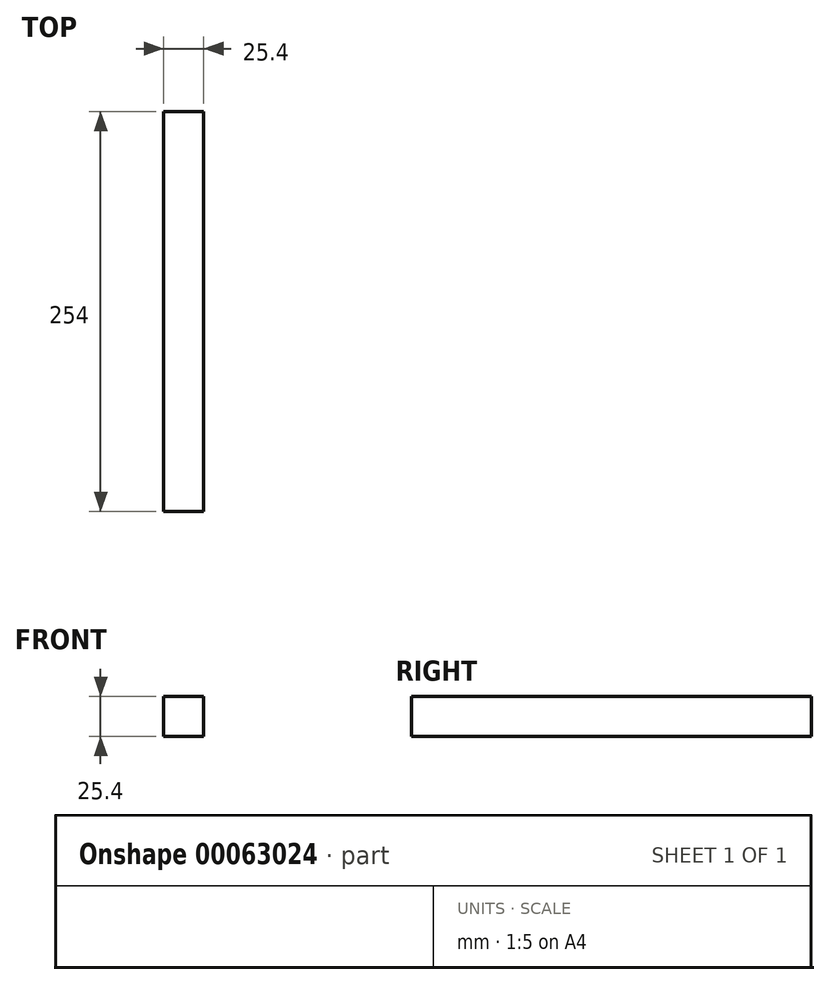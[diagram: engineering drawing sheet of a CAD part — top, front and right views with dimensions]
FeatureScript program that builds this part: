
annotation { "Feature Type Name" : "Feature", "Feature Type Description" : "" }
export const myFeature = defineFeature(function(context is Context, id is Id, definition is map)
    precondition{}
    {
        {
            var Q0;
            Q0=qCreatedBy(makeId("Top.planeOp"),FACE);
            var sketch = newSketch(context, id + "F0", { "sketchPlane" : qUnion([Q0])});
            skLineSegment(sketch, "E0.rect.bottom", {"start": v(12.7, 127) * mm, "end": v(-12.7, 127) * mm});
            skLineSegment(sketch, "E0.rect.top", {"start": v(12.7, -127) * mm, "end": v(-12.7, -127) * mm});
            skLineSegment(sketch, "E0.rect.left", {"start": v(12.7, 127) * mm, "end": v(12.7, -127) * mm});
            skLineSegment(sketch, "E0.rect.right", {"start": v(-12.7, 127) * mm, "end": v(-12.7, -127) * mm});
            skPoint(sketch, "E0.rect.middle", {"position": v(0, 0) * mm});
            skSolve(sketch);
        }
        {
            var Q0;
            Q0 = qSketchRegion(id + "F0", true);
            extrude(context, id + "F1", {"entities" : qUnion([Q0]), "depth" : 25.4 * mm});
        }
    });
